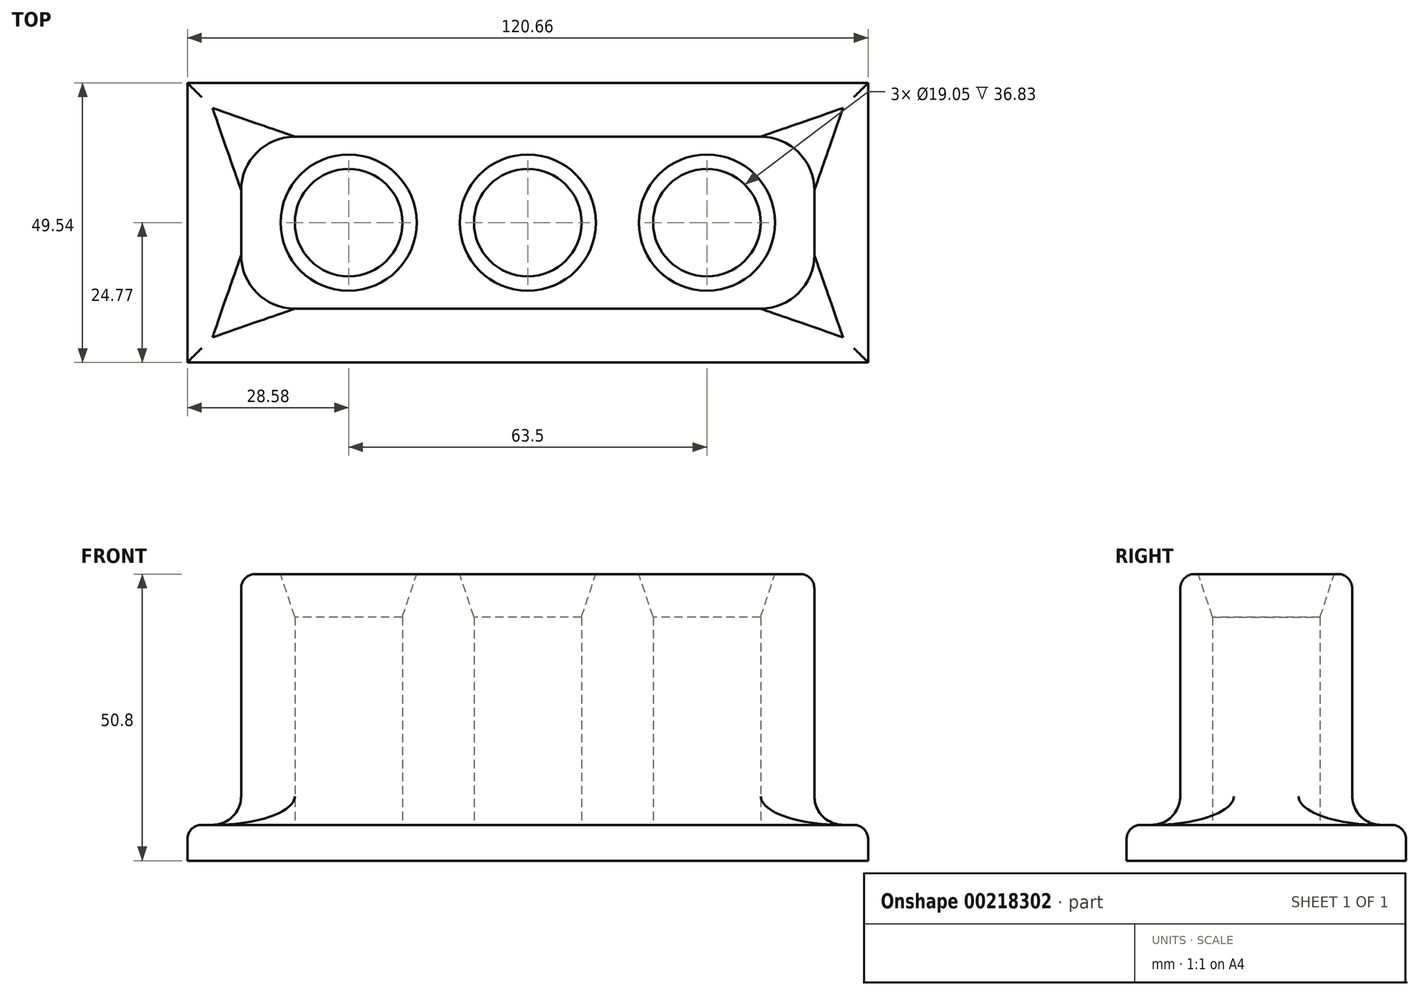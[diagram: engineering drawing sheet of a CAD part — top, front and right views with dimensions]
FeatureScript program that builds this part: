
annotation { "Feature Type Name" : "Feature", "Feature Type Description" : "" }
export const myFeature = defineFeature(function(context is Context, id is Id, definition is map)
    precondition{}
    {
        {
            var Q0;
            Q0=qCreatedBy(makeId("Top.planeOp"),FACE);
            var sketch = newSketch(context, id + "F0", { "sketchPlane" : qUnion([Q0])});
            skLineSegment(sketch, "E0.bottom", {"start": v(50.8, 15.24) * mm, "end": v(-50.8, 15.24) * mm});
            skLineSegment(sketch, "E0.top", {"start": v(50.8, -15.24) * mm, "end": v(-50.8, -15.24) * mm});
            skLineSegment(sketch, "E0.left", {"start": v(50.8, 15.24) * mm, "end": v(50.8, -15.24) * mm});
            skLineSegment(sketch, "E0.right", {"start": v(-50.8, 15.24) * mm, "end": v(-50.8, -15.24) * mm});
            skPoint(sketch, "E0.middle", {"position": v(0, 0) * mm});
            skCircle(sketch, "E1", {"center": v(0, 0) * mm, "radius": 9.53 * mm});
            skCircle(sketch, "E2", {"center": v(-31.75, 0) * mm, "radius": 9.53 * mm});
            skCircle(sketch, "E3", {"center": v(31.75, 0) * mm, "radius": 9.53 * mm});
            skSolve(sketch);
        }
        {
            var Q0;
            Q0=qSketchRegion(id+"F0",true);
            extrude(context, id + "F1", {"entities" : qUnion([Q0]), "depth" : 50.8 * mm});
        }
        {
            var Q0;
            Q0=makeQuery(id+"F0.imprint","IMPRINT",FACE,{"disambiguationData":[TD([[makeQuery(id+"F0.imprint","IMPRINT",EDGE,{"derivedFrom":sQuery(id+"F0.wireOp",EDGE,"E0.bottom")}),1.0]])]});
            var sketch = newSketch(context, id + "F2", { "sketchPlane" : qUnion([Q0])});
            skLineSegment(sketch, "E4.bottom", {"start": v(60.33, -24.77) * mm, "end": v(-60.32, -24.77) * mm});
            skLineSegment(sketch, "E4.top", {"start": v(60.33, 24.77) * mm, "end": v(-60.32, 24.77) * mm});
            skLineSegment(sketch, "E4.left", {"start": v(60.33, -24.77) * mm, "end": v(60.33, 24.77) * mm});
            skLineSegment(sketch, "E4.right", {"start": v(-60.32, -24.77) * mm, "end": v(-60.32, 24.77) * mm});
            skPoint(sketch, "E4.middle", {"position": v(0, 0) * mm});
            skSolve(sketch);
        }
        {
            var Q0;
            Q0=qSketchRegion(id+"F2",true);
            extrude(context, id + "F3", {"entities" : qUnion([Q0]), "operationType" : NewBodyOperationType.ADD, "depth" : 6.35 * mm});
        }
        {
            var Q0;
            Q0=makeQuery(id+"F3.boolean.opBoolean","INTERSECT",EDGE,{"derivedFrom":[makeQuery(id+"F1.opExtrude","SWEPT_FACE",FACE,{"disambiguationData":[OSD([sQuery(id+"F0.wireOp",EDGE,"E0.top")])]}),makeQuery(id+"F3.opExtrude","CAP_FACE",FACE,{"disambiguationData":[OSD([sQuery(id+"F2.wireOp",EDGE,"E4.bottom"),sQuery(id+"F2.wireOp",EDGE,"E4.top"),sQuery(id+"F2.wireOp",EDGE,"E4.left"),sQuery(id+"F2.wireOp",EDGE,"E4.right")])],"isStart":false})]});
            var Q1;
            Q1=makeQuery(id+"F3.boolean.opBoolean","INTERSECT",EDGE,{"derivedFrom":[makeQuery(id+"F1.opExtrude","SWEPT_FACE",FACE,{"disambiguationData":[OSD([sQuery(id+"F0.wireOp",EDGE,"E0.left")])]}),makeQuery(id+"F3.opExtrude","CAP_FACE",FACE,{"disambiguationData":[OSD([sQuery(id+"F2.wireOp",EDGE,"E4.bottom"),sQuery(id+"F2.wireOp",EDGE,"E4.top"),sQuery(id+"F2.wireOp",EDGE,"E4.left"),sQuery(id+"F2.wireOp",EDGE,"E4.right")])],"isStart":false})]});
            var Q2;
            Q2=makeQuery(id+"F3.boolean.opBoolean","INTERSECT",EDGE,{"derivedFrom":[makeQuery(id+"F1.opExtrude","SWEPT_FACE",FACE,{"disambiguationData":[OSD([sQuery(id+"F0.wireOp",EDGE,"E0.bottom")])]}),makeQuery(id+"F3.opExtrude","CAP_FACE",FACE,{"disambiguationData":[OSD([sQuery(id+"F2.wireOp",EDGE,"E4.bottom"),sQuery(id+"F2.wireOp",EDGE,"E4.top"),sQuery(id+"F2.wireOp",EDGE,"E4.left"),sQuery(id+"F2.wireOp",EDGE,"E4.right")])],"isStart":false})]});
            var Q3;
            Q3=makeQuery(id+"F3.boolean.opBoolean","INTERSECT",EDGE,{"derivedFrom":[makeQuery(id+"F1.opExtrude","SWEPT_FACE",FACE,{"disambiguationData":[OSD([sQuery(id+"F0.wireOp",EDGE,"E0.right")])]}),makeQuery(id+"F3.opExtrude","CAP_FACE",FACE,{"disambiguationData":[OSD([sQuery(id+"F2.wireOp",EDGE,"E4.bottom"),sQuery(id+"F2.wireOp",EDGE,"E4.top"),sQuery(id+"F2.wireOp",EDGE,"E4.left"),sQuery(id+"F2.wireOp",EDGE,"E4.right")])],"isStart":false})]});
            fillet(context, id + "F4", {"entities" : qUnion([Q0, Q1, Q2, Q3]), "radius" : 5.08 * mm, "tangentPropagation" : true, "allowEdgeOverflow" : false});
        }
        {
            var Q0;
            Q0=makeQuery(id+"F3.opExtrude","CAP_EDGE",EDGE,{"disambiguationData":[OSD([sQuery(id+"F2.wireOp",EDGE,"E4.bottom")])],"isStart":false});
            var Q1;
            Q1=makeQuery(id+"F3.opExtrude","CAP_EDGE",EDGE,{"disambiguationData":[OSD([sQuery(id+"F2.wireOp",EDGE,"E4.left")])],"isStart":false});
            var Q2;
            Q2=makeQuery(id+"F3.opExtrude","CAP_EDGE",EDGE,{"disambiguationData":[OSD([sQuery(id+"F2.wireOp",EDGE,"E4.right")])],"isStart":false});
            var Q3;
            Q3=makeQuery(id+"F3.opExtrude","CAP_EDGE",EDGE,{"disambiguationData":[OSD([sQuery(id+"F2.wireOp",EDGE,"E4.top")])],"isStart":false});
            fillet(context, id + "F5", {"entities" : qUnion([Q0, Q1, Q2, Q3]), "radius" : 2.54 * mm, "tangentPropagation" : true, "allowEdgeOverflow" : false});
        }
        {
            var Q0;
            Q0=makeQuery(id+"F1.opExtrude","SWEPT_EDGE",EDGE,{"disambiguationData":[OSD([sQuery(id+"F0.wireOp",EDGE,"E0.top"),sQuery(id+"F0.wireOp",EDGE,"E0.right")])]});
            var Q1;
            Q1=makeQuery(id+"F1.opExtrude","SWEPT_EDGE",EDGE,{"disambiguationData":[OSD([sQuery(id+"F0.wireOp",EDGE,"E0.top"),sQuery(id+"F0.wireOp",EDGE,"E0.left")])]});
            var Q2;
            Q2=makeQuery(id+"F1.opExtrude","SWEPT_EDGE",EDGE,{"disambiguationData":[OSD([sQuery(id+"F0.wireOp",EDGE,"E0.bottom"),sQuery(id+"F0.wireOp",EDGE,"E0.left")])]});
            var Q3;
            Q3=makeQuery(id+"F1.opExtrude","SWEPT_EDGE",EDGE,{"disambiguationData":[OSD([sQuery(id+"F0.wireOp",EDGE,"E0.bottom"),sQuery(id+"F0.wireOp",EDGE,"E0.right")])]});
            fillet(context, id + "F6", {"entities" : qUnion([Q0, Q1, Q2, Q3]), "radius" : 9.52 * mm, "tangentPropagation" : true, "allowEdgeOverflow" : false});
        }
        {
            var Q0;
            Q0=makeQuery(id+"F1.opExtrude","CAP_EDGE",EDGE,{"disambiguationData":[OSD([sQuery(id+"F0.wireOp",EDGE,"E0.top")])],"isStart":false});
            fillet(context, id + "F7", {"entities" : qUnion([Q0]), "radius" : 2.54 * mm, "tangentPropagation" : true, "allowEdgeOverflow" : false});
        }
        {
            var Q0;
            Q0=makeQuery(id+"F1.opExtrude","CAP_EDGE",EDGE,{"disambiguationData":[OSD([sQuery(id+"F0.wireOp",EDGE,"E2")])],"isStart":false});
            var Q1;
            Q1=makeQuery(id+"F1.opExtrude","CAP_EDGE",EDGE,{"disambiguationData":[OSD([sQuery(id+"F0.wireOp",EDGE,"E1")])],"isStart":false});
            var Q2;
            Q2=makeQuery(id+"F1.opExtrude","CAP_EDGE",EDGE,{"disambiguationData":[OSD([sQuery(id+"F0.wireOp",EDGE,"E3")])],"isStart":false});
            chamfer(context, id + "F8", {"entities" : qUnion([Q0, Q1, Q2]), "chamferType" : ChamferType.TWO_OFFSETS, "width1" : 7.62 * mm, "oppositeDirection" : false, "width2" : 2.54 * mm, "tangentPropagation" : true});
        }
    });
